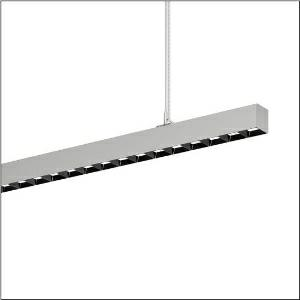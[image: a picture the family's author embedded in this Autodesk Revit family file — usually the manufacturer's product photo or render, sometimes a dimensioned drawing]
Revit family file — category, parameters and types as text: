
# Revit family: silica_r__21_51mx31dc4dsb_9913
name_source: partatom
category: Lighting Fixtures
units: mm (PartAtom-declared; Revit-internal decimal feet)

## family parameters
Cut with Voids When Loaded = No
Host = Face
Light Source = No
Part Type = Normal
Room Calculation Point = No
Round Connector Dimension = Use Diameter
Shared = No

## types (1)
- --- (1 x LED, 18230 lm, 105.9 W, 4000K)
    Apparent Load = 106 VA
    CIE Flux Codes = 87 99 100 59 100
    Color Rendering = 80
    Color Temperature = 4000K
    Default Elevation = 1800 mm
    Description = Silica® 21, office luminaire, primary light control with darklight reflector, of PMMA, black, CAT 2 (L<= 3000cd/m²), light emission: direct/indirect distribution, primary light characteristic: symmetric, installation type: suspended mounting, LED, rated luminous flux: 18.230lm, luminous efficacy: 172lm/W, light colour: 840, colour temperature: 4000K, control gear: DALI 2, with terminal, 3+2-pole, max. 2.5mm², mains connection: 220..240V, AC, 50/60Hz, rated input power: 105.9W, luminaire housing, of aluminium, metallic grey (RAL 9006), length: 3.004mm, width: 53mm, height: 53mm, protection rating (complete): IP20, insulation class (complete): insulation class I (protective earthing), certification: CE, permissible operating ambient temperature: 0..+35°C, standard: EN 50419, packaging unit: 1 piece
    Height = 53 mm
    Lamp = 1 x LED
    Lamp Light Flux = 18230 lm
    Lamp Power = 105.9 W
    Lamp count = 1
    Length = 3004 mm
    Luminous efficacy = 172 lm/W
    Manufacturer = Siteco
    ModVariant = No
    Model = 51MX31DC4DSB
    Mounting Place = Ceiling
    Mounting Type = Pendant
    Number of Poles = 1
    OnlyDefault = Yes
    Power Factor = 1
    Product Name = Silica® 21
    Product group = office luminaire | ceiling pendant
    ProductGroupID = 904
    Protection Class = Protection class I
    Protection Degree = IP 20
    RLX_Detail_Level = 1
    RLX_Emergency_Light_Flux = 0 lm
    RLX_Emergency_Type = 0
    RLX_Emergency_Type_DB = No
    RlxData = <blob elided: 65845 chars, md5=65d872ad>
    Socket = socket
    Standby Power = 0 W
    System Light Flux = 18230 lm
    System Power = 106 W
    Type Comments = factory setting: luminous flux: 100 % | dim-lin: 254 | 367 mA
    Type Image = l_1335859.jpg
    URL = http://relux.com
    VarID = @adj_120976
    Voltage = 0 V
    Weight = 0.00 kg
    Width = 53 mm

## geometry (parser evidence)
native form markers: Blend x4, Sweep x11
no freeform markers — native parametric forms only
